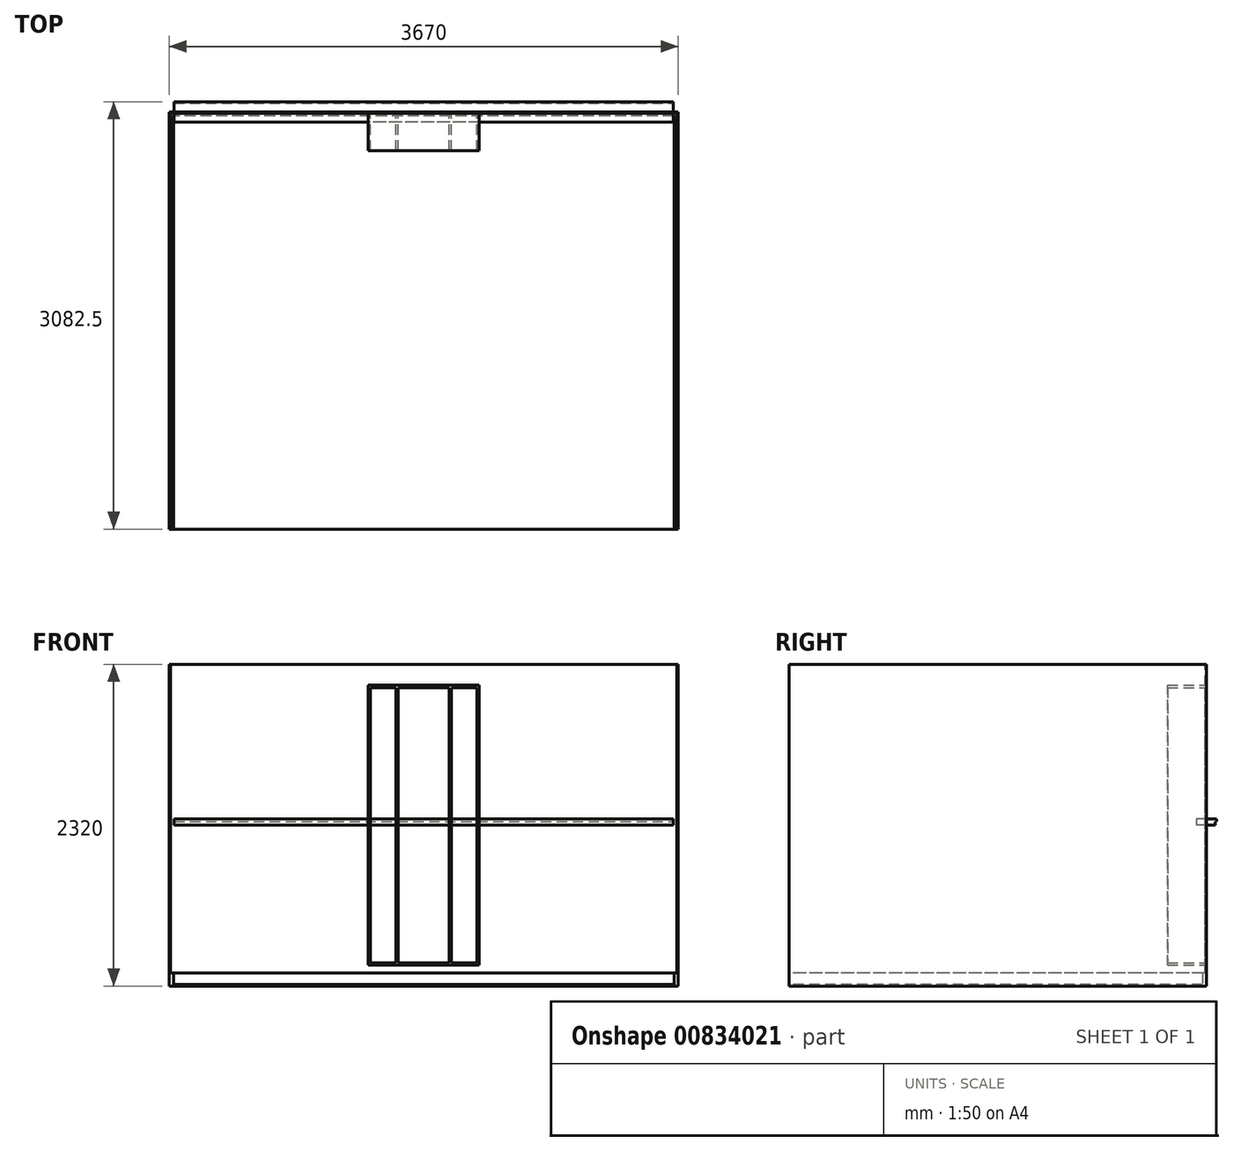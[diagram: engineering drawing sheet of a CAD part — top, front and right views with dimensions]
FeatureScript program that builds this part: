
annotation { "Feature Type Name" : "Feature", "Feature Type Description" : "" }
export const myFeature = defineFeature(function(context is Context, id is Id, definition is map)
    precondition{}
    {
        {
            var Q0;
            Q0=qCreatedBy(makeId("Front.planeOp"),FACE);
            var sketch = newSketch(context, id + "F0", { "sketchPlane" : qUnion([Q0])});
            skLineSegment(sketch, "E0.bottom", {"start": v(200, 1010) * mm, "end": v(-200, 1010) * mm});
            skLineSegment(sketch, "E0.top", {"start": v(200, -1010) * mm, "end": v(-200, -1010) * mm});
            skLineSegment(sketch, "E0.left", {"start": v(200, 1010) * mm, "end": v(200, -1010) * mm});
            skLineSegment(sketch, "E0.right", {"start": v(-200, 1010) * mm, "end": v(-200, -1010) * mm});
            skPoint(sketch, "E0.middle", {"position": v(0, 0) * mm});
            skLineSegment(sketch, "E1.bottom", {"start": v(183, 993) * mm, "end": v(-183, 993) * mm});
            skLineSegment(sketch, "E1.top", {"start": v(183, -993) * mm, "end": v(-183, -993) * mm});
            skLineSegment(sketch, "E1.left", {"start": v(183, 993) * mm, "end": v(183, -993) * mm});
            skLineSegment(sketch, "E1.right", {"start": v(-183, 993) * mm, "end": v(-183, -993) * mm});
            skSolve(sketch);
        }
        {
            var Q0;
            Q0 = qSketchRegion(id + "F0", true);
            extrude(context, id + "F1", {"entities" : qUnion([Q0]), "depth" : 280 * mm, "offsetDistance" : 25 * mm});
        }
        {
            var Q0;
            Q0=makeQuery(id+"F1.opExtrude","SWEPT_FACE",FACE,{"disambiguationData":[OSD([sQuery(id+"F0.wireOp",EDGE,"E1.right")])]});
            var sketch = newSketch(context, id + "F2", { "sketchPlane" : qUnion([Q0])});
            skLineSegment(sketch, "E2.bottom", {"start": v(-14, -993) * mm, "end": v(-10, -993) * mm});
            skLineSegment(sketch, "E2.top", {"start": v(-14, 993) * mm, "end": v(-10, 993) * mm});
            skLineSegment(sketch, "E2.left", {"start": v(-14, -993) * mm, "end": v(-14, 993) * mm});
            skLineSegment(sketch, "E2.right", {"start": v(-10, -993) * mm, "end": v(-10, 993) * mm});
            skSolve(sketch);
        }
        {
            var Q0;
            Q0 = qSketchRegion(id + "F2", true);
            extrude(context, id + "F3", {"entities" : qUnion([Q0]), "operationType" : NewBodyOperationType.ADD, "endBound" : BoundingType.UP_TO_NEXT, "depth" : 25 * mm, "offsetDistance" : 25 * mm});
        }
        {
            var Q0;
            Q0=qCreatedBy(makeId("Front.planeOp"),FACE);
            var sketch = newSketch(context, id + "F4", { "sketchPlane" : qUnion([Q0])});
            skLineSegment(sketch, "E3.bottom", {"start": v(400, -1010) * mm, "end": v(-400, -1010) * mm});
            skLineSegment(sketch, "E3.top", {"start": v(400, 1010) * mm, "end": v(-400, 1010) * mm});
            skLineSegment(sketch, "E3.left", {"start": v(400, -1010) * mm, "end": v(400, 1010) * mm});
            skLineSegment(sketch, "E3.right", {"start": v(-400, -1010) * mm, "end": v(-400, 1010) * mm});
            skPoint(sketch, "E3.middle", {"position": v(0, 0) * mm});
            skLineSegment(sketch, "E4.bottom", {"start": v(383, -993) * mm, "end": v(-383, -993) * mm});
            skLineSegment(sketch, "E4.top", {"start": v(383, 993) * mm, "end": v(-383, 993) * mm});
            skLineSegment(sketch, "E4.left", {"start": v(383, -993) * mm, "end": v(383, 993) * mm});
            skLineSegment(sketch, "E4.right", {"start": v(-383, -993) * mm, "end": v(-383, 993) * mm});
            skSolve(sketch);
        }
        {
            var Q0;
            Q0 = qSketchRegion(id + "F4", true);
            extrude(context, id + "F5", {"entities" : qUnion([Q0]), "depth" : 280 * mm, "offsetDistance" : 25 * mm});
        }
        {
            var Q0;
            Q0 = qSketchRegion(id + "F2", true);
            var Q1;
            Q1=makeQuery(id+"F5.opExtrude","SWEPT_FACE",FACE,{"disambiguationData":[OSD([sQuery(id+"F4.wireOp",EDGE,"E4.left")])]});
            var Q2;
            Q2=makeQuery(id+"F5.opExtrude","SWEPT_FACE",FACE,{"disambiguationData":[OSD([sQuery(id+"F4.wireOp",EDGE,"E4.right")])]});
            extrude(context, id + "F6", {"entities" : qUnion([Q0]), "operationType" : NewBodyOperationType.ADD, "endBound" : BoundingType.UP_TO_SURFACE, "depth" : 25 * mm, "endBoundEntityFace" : qUnion([Q1]), "offsetDistance" : 25 * mm, "hasSecondDirection" : true, "secondDirectionBound" : SecondDirectionBoundingType.UP_TO_SURFACE, "secondDirectionOppositeDirection" : true, "secondDirectionDepth" : 25 * mm, "secondDirectionBoundEntityFace" : qUnion([Q2])});
        }
        {
            var Q0;
            Q0=qCreatedBy(makeId("Front.planeOp"),FACE);
            var sketch = newSketch(context, id + "F7", { "sketchPlane" : qUnion([Q0])});
            skLineSegment(sketch, "E5.bottom", {"start": v(1835, -1160) * mm, "end": v(-1835, -1160) * mm});
            skLineSegment(sketch, "E5.top", {"start": v(1835, 1160) * mm, "end": v(-1835, 1160) * mm});
            skLineSegment(sketch, "E5.left", {"start": v(1835, -1160) * mm, "end": v(1835, 1160) * mm});
            skLineSegment(sketch, "E5.right", {"start": v(-1835, -1160) * mm, "end": v(-1835, 1160) * mm});
            skPoint(sketch, "E5.middle", {"position": v(0, 0) * mm});
            skSolve(sketch);
        }
        {
            var Q0;
            Q0 = qSketchRegion(id + "F7", true);
            extrude(context, id + "F8", {"entities" : qUnion([Q0]), "depth" : 10 * mm, "offsetDistance" : 25 * mm});
        }
        {
            var Q0;
            Q0=makeQuery(id+"F8.opExtrude","CAP_FACE",FACE,{"disambiguationData":[OSD([sQuery(id+"F7.wireOp",EDGE,"E5.bottom"),sQuery(id+"F7.wireOp",EDGE,"E5.top"),sQuery(id+"F7.wireOp",EDGE,"E5.left"),sQuery(id+"F7.wireOp",EDGE,"E5.right")])],"isStart":false});
            var sketch = newSketch(context, id + "F9", { "sketchPlane" : qUnion([Q0])});
            skLineSegment(sketch, "E6", {"start": v(-1835, 1160) * mm, "end": v(-1825, 1160) * mm});
            skLineSegment(sketch, "E7", {"start": v(-1825, 1160) * mm, "end": v(-1825, -1150) * mm});
            skLineSegment(sketch, "E8", {"start": v(-1825, -1150) * mm, "end": v(1825, -1150) * mm});
            skLineSegment(sketch, "E9", {"start": v(1825, -1150) * mm, "end": v(1825, 1160) * mm});
            skLineSegment(sketch, "E10", {"start": v(1825, 1160) * mm, "end": v(1835, 1160) * mm});
            skLineSegment(sketch, "E11", {"start": v(1835, 1160) * mm, "end": v(1835, -1160) * mm});
            skLineSegment(sketch, "E12", {"start": v(1835, -1160) * mm, "end": v(-1835, -1160) * mm});
            skLineSegment(sketch, "E13", {"start": v(-1835, -1160) * mm, "end": v(-1835, 1160) * mm});
            skSolve(sketch);
        }
        {
            var Q0;
            Q0 = qSketchRegion(id + "F9", true);
            extrude(context, id + "F10", {"entities" : qUnion([Q0]), "operationType" : NewBodyOperationType.ADD, "depth" : 3000 * mm, "offsetDistance" : 25 * mm});
        }
        {
            var Q0;
            Q0=makeQuery(id+"F10.opExtrude","CAP_FACE",FACE,{"disambiguationData":[OSD([sQuery(id+"F9.wireOp",EDGE,"E6"),sQuery(id+"F9.wireOp",EDGE,"E7"),sQuery(id+"F9.wireOp",EDGE,"E8"),sQuery(id+"F9.wireOp",EDGE,"E9"),sQuery(id+"F9.wireOp",EDGE,"E10"),sQuery(id+"F9.wireOp",EDGE,"E11"),sQuery(id+"F9.wireOp",EDGE,"E12"),sQuery(id+"F9.wireOp",EDGE,"E13")])],"isStart":false});
            var sketch = newSketch(context, id + "F11", { "sketchPlane" : qUnion([Q0])});
            skLineSegment(sketch, "E14.bottom", {"start": v(-1825, -1065) * mm, "end": v(-1805, -1065) * mm});
            skLineSegment(sketch, "E14.top", {"start": v(-1825, -1150) * mm, "end": v(-1805, -1150) * mm});
            skLineSegment(sketch, "E14.left", {"start": v(-1825, -1065) * mm, "end": v(-1825, -1150) * mm});
            skLineSegment(sketch, "E14.right", {"start": v(-1805, -1065) * mm, "end": v(-1805, -1150) * mm});
            skLineSegment(sketch, "E15", {"start": v(0, 0) * mm, "end": v(0, -1150) * mm, "construction": true});
            skLineSegment(sketch, "E16.MirrorCS", {"start": v(1825, -1065) * mm, "end": v(1805, -1065) * mm});
            skLineSegment(sketch, "E17.MirrorCS", {"start": v(1825, -1150) * mm, "end": v(1805, -1150) * mm});
            skLineSegment(sketch, "E18.MirrorCS", {"start": v(1805, -1065) * mm, "end": v(1805, -1150) * mm});
            skLineSegment(sketch, "E19.MirrorCS", {"start": v(1825, -1065) * mm, "end": v(1825, -1150) * mm});
            skSolve(sketch);
        }
        {
            var Q0;
            Q0 = qSketchRegion(id + "F11", true);
            var Q1;
            Q1=makeQuery(id+"F8.opExtrude","CAP_FACE",FACE,{"disambiguationData":[OSD([sQuery(id+"F7.wireOp",EDGE,"E5.bottom"),sQuery(id+"F7.wireOp",EDGE,"E5.top"),sQuery(id+"F7.wireOp",EDGE,"E5.left"),sQuery(id+"F7.wireOp",EDGE,"E5.right")])],"isStart":false});
            extrude(context, id + "F12", {"entities" : qUnion([Q0]), "operationType" : NewBodyOperationType.ADD, "endBound" : BoundingType.UP_TO_SURFACE, "oppositeDirection" : true, "depth" : 25 * mm, "endBoundEntityFace" : qUnion([Q1]), "offsetDistance" : 25 * mm});
        }
        {
            var Q0;
            Q0=makeQuery(id+"F12.opExtrude","SWEPT_FACE",FACE,{"disambiguationData":[OSD([sQuery(id+"F11.wireOp",EDGE,"E14.right")])]});
            var sketch = newSketch(context, id + "F13", { "sketchPlane" : qUnion([Q0])});
            skLineSegment(sketch, "E20.bottom", {"start": v(-30, -1065) * mm, "end": v(-10, -1065) * mm});
            skLineSegment(sketch, "E20.top", {"start": v(-30, -1150) * mm, "end": v(-10, -1150) * mm});
            skLineSegment(sketch, "E20.left", {"start": v(-30, -1065) * mm, "end": v(-30, -1150) * mm});
            skLineSegment(sketch, "E20.right", {"start": v(-10, -1065) * mm, "end": v(-10, -1150) * mm});
            skSolve(sketch);
        }
        {
            var Q0;
            Q0 = qSketchRegion(id + "F13", true);
            extrude(context, id + "F14", {"entities" : qUnion([Q0]), "operationType" : NewBodyOperationType.ADD, "endBound" : BoundingType.UP_TO_NEXT, "depth" : 25 * mm, "offsetDistance" : 25 * mm});
        }
        {
            var Q0;
            Q0=qCreatedBy(makeId("Top.planeOp"),FACE);
            var sketch = newSketch(context, id + "F15", { "sketchPlane" : qUnion([Q0])});
            skLineSegment(sketch, "E21.bottom", {"start": v(1800, 72.5) * mm, "end": v(-1800, 72.5) * mm});
            skLineSegment(sketch, "E21.top", {"start": v(1800, -72.5) * mm, "end": v(-1800, -72.5) * mm});
            skLineSegment(sketch, "E21.left", {"start": v(1800, 72.5) * mm, "end": v(1800, -72.5) * mm});
            skLineSegment(sketch, "E21.right", {"start": v(-1800, 72.5) * mm, "end": v(-1800, -72.5) * mm});
            skPoint(sketch, "E21.middle", {"position": v(0, 0) * mm});
            skSolve(sketch);
        }
        {
            var Q0;
            Q0 = qSketchRegion(id + "F15", true);
            extrude(context, id + "F16", {"entities" : qUnion([Q0]), "depth" : 45 * mm, "offsetDistance" : 25 * mm});
        }
        {
            var Q0;
            Q0=makeQuery(id+"F16.opExtrude","SWEPT_FACE",FACE,{"disambiguationData":[OSD([sQuery(id+"F15.wireOp",EDGE,"E21.left")])]});
            var sketch = newSketch(context, id + "F17", { "sketchPlane" : qUnion([Q0])});
            skLineSegment(sketch, "E22.bottom", {"start": v(72.5, 0) * mm, "end": v(62.5, 0) * mm});
            skLineSegment(sketch, "E22.top", {"start": v(72.5, 25) * mm, "end": v(62.5, 25) * mm});
            skLineSegment(sketch, "E22.left", {"start": v(72.5, 0) * mm, "end": v(72.5, 25) * mm});
            skLineSegment(sketch, "E22.right", {"start": v(62.5, 0) * mm, "end": v(62.5, 25) * mm});
            skSolve(sketch);
        }
        {
            var Q0;
            Q0 = qSketchRegion(id + "F17", true);
            extrude(context, id + "F18", {"entities" : qUnion([Q0]), "operationType" : NewBodyOperationType.REMOVE, "endBound" : BoundingType.UP_TO_NEXT, "oppositeDirection" : true, "depth" : 25 * mm, "offsetDistance" : 25 * mm});
        }
    });
